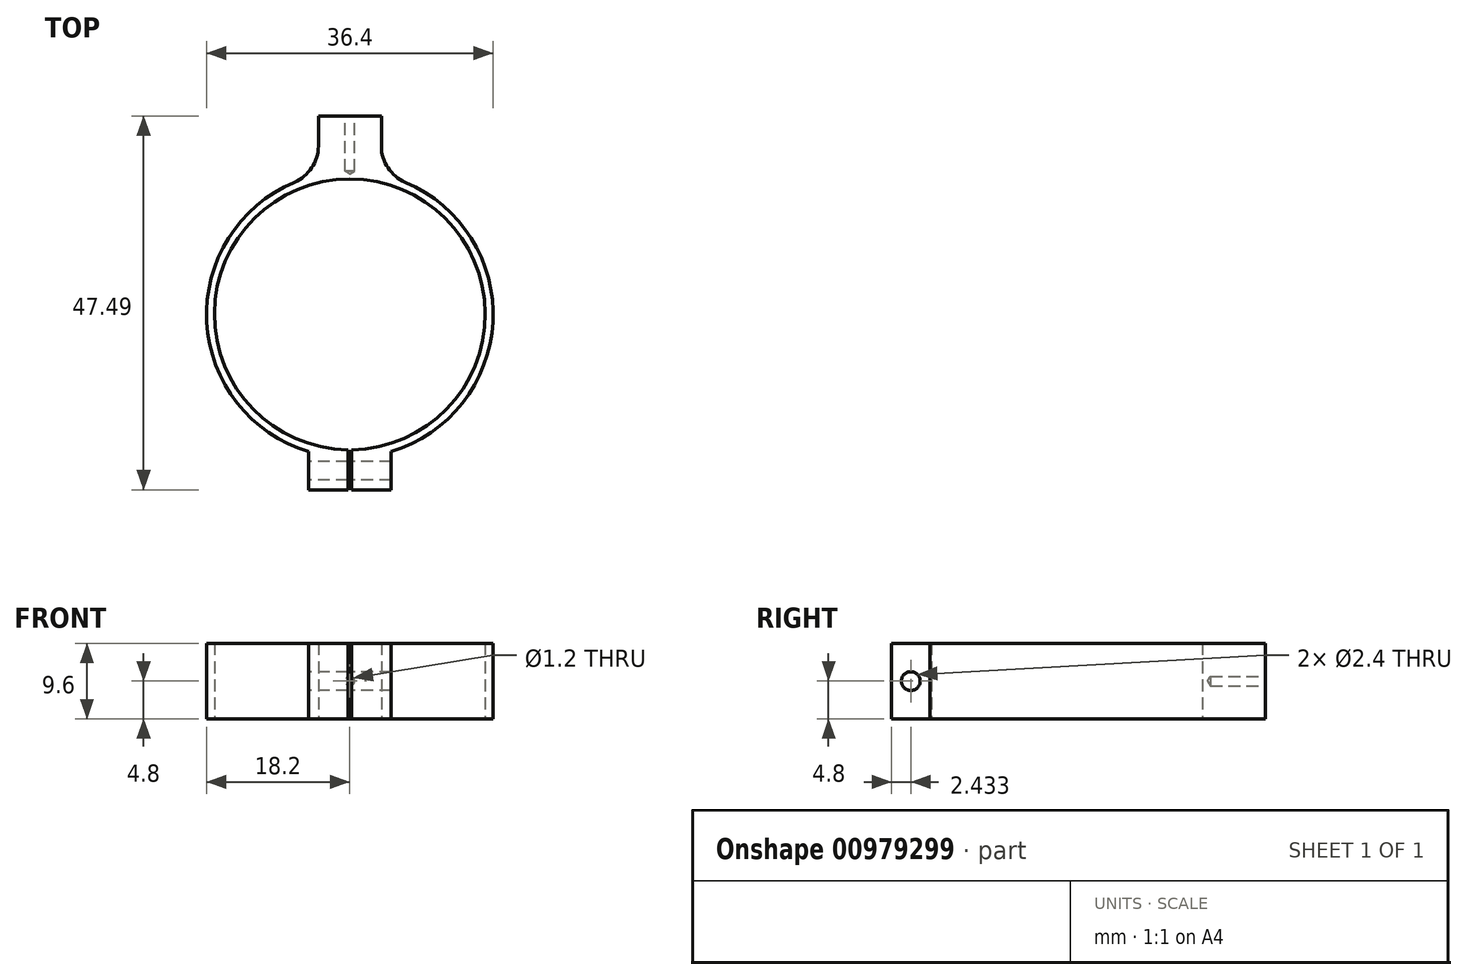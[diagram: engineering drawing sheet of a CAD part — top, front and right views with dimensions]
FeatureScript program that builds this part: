
annotation { "Feature Type Name" : "Feature", "Feature Type Description" : "" }
export const myFeature = defineFeature(function(context is Context, id is Id, definition is map)
    precondition{}
    {
        {
            var Q0;
            Q0=qCreatedBy(makeId("Top.planeOp"),FACE);
            var sketch = newSketch(context, id + "F0", { "sketchPlane" : qUnion([Q0])});
            skCircle(sketch, "E0", {"center": v(0, 0) * mm, "radius": 17.2 * mm});
            skArc(sketch, "E1.0", {"start": v(0.25, -18.2) * mm, "mid": v(0, 18.2) * mm, "end": v(-0.25, -18.2) * mm});
            skLineSegment(sketch, "E2", {"start": v(-4, 17.75) * mm, "end": v(-4, 25.2) * mm});
            skLineSegment(sketch, "E3", {"start": v(-4, 25.2) * mm, "end": v(4, 25.2) * mm});
            skLineSegment(sketch, "E4", {"start": v(4, 25.2) * mm, "end": v(4, 17.75) * mm});
            skLineSegment(sketch, "E5", {"start": v(0, 18.2) * mm, "end": v(0, 25.2) * mm, "construction": true});
            skLineSegment(sketch, "E6", {"start": v(-0.25, -18.2) * mm, "end": v(-0.25, -22.29) * mm});
            skLineSegment(sketch, "E7", {"start": v(-0.25, -22.29) * mm, "end": v(-5.25, -22.29) * mm});
            skLineSegment(sketch, "E8", {"start": v(-5.25, -22.29) * mm, "end": v(-5.25, -17.43) * mm});
            skLineSegment(sketch, "E9.MirrorCS", {"start": v(0.25, -18.2) * mm, "end": v(0.25, -22.29) * mm});
            skLineSegment(sketch, "E10.MirrorCS", {"start": v(0.25, -22.29) * mm, "end": v(5.25, -22.29) * mm});
            skLineSegment(sketch, "E11.MirrorCS", {"start": v(5.25, -22.29) * mm, "end": v(5.25, -17.43) * mm});
            skLineSegment(sketch, "E12", {"start": v(-0.25, -22.29) * mm, "end": v(0.25, -22.29) * mm, "construction": true});
            skLineSegment(sketch, "E13", {"start": v(-0.25, -18.2) * mm, "end": v(-0.25, -17.2) * mm});
            skLineSegment(sketch, "E14", {"start": v(0.25, -18.2) * mm, "end": v(0.25, -17.2) * mm});
            skSolve(sketch);
        }
        {
            var Q0;
            {var subQ0=sQuery(id+"F0.wireOp",EDGE,"E2");Q0=makeQuery(id+"F0.imprint","IMPRINT",FACE,{"disambiguationData":[TD([[makeQuery(id+"F0.imprint","IMPRINT",EDGE,{"derivedFrom":subQ0}),-1.0]])]});}
            var Q1;
            {var subQ5=sQuery(id+"F0.wireOp",EDGE,"E13");Q1=makeQuery(id+"F0.imprint","IMPRINT",FACE,{"disambiguationData":[TD([[makeQuery(id+"F0.imprint","IMPRINT",EDGE,{"derivedFrom":subQ5}),1.0]])]});}
            var Q2;
            {var subQ0=sQuery(id+"F0.wireOp",EDGE,"E6");Q2=makeQuery(id+"F0.imprint","IMPRINT",FACE,{"disambiguationData":[TD([[makeQuery(id+"F0.imprint","IMPRINT",EDGE,{"derivedFrom":subQ0}),-1.0]])]});}
            var Q3;
            {var subQ0=sQuery(id+"F0.wireOp",EDGE,"E9.MirrorCS");Q3=makeQuery(id+"F0.imprint","IMPRINT",FACE,{"disambiguationData":[TD([[makeQuery(id+"F0.imprint","IMPRINT",EDGE,{"derivedFrom":subQ0}),1.0]])]});}
            extrude(context, id + "F1", {"entities" : qUnion([Q0, Q1, Q2, Q3]), "depth" : 9.6 * mm, "offsetDistance" : 25 * mm});
        }
        {
            var Q0;
            Q0=makeQuery(id+"F1.opExtrude","SWEPT_FACE",FACE,{"disambiguationData":[OSD([sQuery(id+"F0.wireOp",EDGE,"E8")])]});
            var sketch = newSketch(context, id + "F2", { "sketchPlane" : qUnion([Q0])});
            skLineSegment(sketch, "E15", {"start": v(19.86, 9.6) * mm, "end": v(19.86, 0) * mm, "construction": true});
            skPoint(sketch, "E16", {"position": v(19.86, 4.8) * mm});
            skSolve(sketch);
        }
        {
            var Q0;
            Q0=sQuery(id+"F2.wireOp",VERTEX,"E16");
            var Q1;
            Q1=makeQuery(id+"F1.opExtrude","SWEPT_BODY",BODY,{"disambiguationData":[OSD([sQuery(id+"F0.wireOp",EDGE,"E0"),sQuery(id+"F0.wireOp",EDGE,"E1.0"),sQuery(id+"F0.wireOp",EDGE,"E2"),sQuery(id+"F0.wireOp",EDGE,"E3"),sQuery(id+"F0.wireOp",EDGE,"E4"),sQuery(id+"F0.wireOp",EDGE,"E6"),sQuery(id+"F0.wireOp",EDGE,"E7"),sQuery(id+"F0.wireOp",EDGE,"E8"),sQuery(id+"F0.wireOp",EDGE,"E9.MirrorCS"),sQuery(id+"F0.wireOp",EDGE,"E10.MirrorCS"),sQuery(id+"F0.wireOp",EDGE,"E11.MirrorCS"),sQuery(id+"F0.wireOp",EDGE,"E13"),sQuery(id+"F0.wireOp",EDGE,"E14")])]});
            hole(context, id + "F3", {"style" : HoleStyle.SIMPLE, "endStyle" : HoleEndStyle.THROUGH, "standardTappedOrClearance" : lookupTablePath({ "fit" : "Normal", "standard" : "ISO", "size" : "M2", "type" : "Clearance" }), "standardBlindInLast" : lookupTablePath({ "fit" : "Normal", "standard" : "ISO", "engagement" : "75%", "pitch" : "0.25 mm", "size" : "M2", "type" : "Clearance & tapped" }), "holeDiameter" : 2.4 * mm, "majorDiameter" : 5 * mm, "isTappedThrough" : true, "tappedDepth" : 12 * mm, "tapClearance" : 3, "locations" : qUnion([Q0]), "scope" : qUnion([Q1])});
        }
        {
            var Q0;
            Q0=makeQuery(id+"F1.opExtrude","SWEPT_FACE",FACE,{"disambiguationData":[OSD([sQuery(id+"F0.wireOp",EDGE,"E3")])]});
            var sketch = newSketch(context, id + "F4", { "sketchPlane" : qUnion([Q0])});
            skLineSegment(sketch, "E17", {"start": v(0, 0) * mm, "end": v(0, 9.6) * mm, "construction": true});
            skPoint(sketch, "E18", {"position": v(0, 4.8) * mm});
            skSolve(sketch);
        }
        {
            var Q0;
            Q0=sQuery(id+"F4.wireOp",VERTEX,"E18");
            var Q1;
            Q1=makeQuery(id+"F1.opExtrude","SWEPT_BODY",BODY,{"disambiguationData":[OSD([sQuery(id+"F0.wireOp",EDGE,"E0"),sQuery(id+"F0.wireOp",EDGE,"E1.0"),sQuery(id+"F0.wireOp",EDGE,"E2"),sQuery(id+"F0.wireOp",EDGE,"E3"),sQuery(id+"F0.wireOp",EDGE,"E4"),sQuery(id+"F0.wireOp",EDGE,"E6"),sQuery(id+"F0.wireOp",EDGE,"E7"),sQuery(id+"F0.wireOp",EDGE,"E8"),sQuery(id+"F0.wireOp",EDGE,"E9.MirrorCS"),sQuery(id+"F0.wireOp",EDGE,"E10.MirrorCS"),sQuery(id+"F0.wireOp",EDGE,"E11.MirrorCS"),sQuery(id+"F0.wireOp",EDGE,"E13"),sQuery(id+"F0.wireOp",EDGE,"E14")])]});
            hole(context, id + "F5", {"style" : HoleStyle.SIMPLE, "endStyle" : HoleEndStyle.BLIND, "standardTappedOrClearance" : lookupTablePath({ "fit" : "Normal", "standard" : "ISO", "size" : "M1", "type" : "Clearance" }), "standardBlindInLast" : lookupTablePath({ "fit" : "Normal", "standard" : "ISO", "engagement" : "75%", "pitch" : "0.2 mm", "size" : "M1", "type" : "Clearance & tapped" }), "holeDiameter" : 1.2 * mm, "majorDiameter" : 5 * mm, "holeDepth" : 7 * mm, "isTappedThrough" : true, "tappedDepth" : 12 * mm, "tapClearance" : 3, "locations" : qUnion([Q0]), "scope" : qUnion([Q1])});
        }
        {
            var Q0;
            Q0=makeQuery(id+"F1.opExtrude","SWEPT_EDGE",EDGE,{"disambiguationData":[OSD([sQuery(id+"F0.wireOp",EDGE,"E1.0"),sQuery(id+"F0.wireOp",EDGE,"E2")])]});
            var Q1;
            Q1=makeQuery(id+"F1.opExtrude","SWEPT_EDGE",EDGE,{"disambiguationData":[OSD([sQuery(id+"F0.wireOp",EDGE,"E1.0"),sQuery(id+"F0.wireOp",EDGE,"E4")])]});
            fillet(context, id + "F6", {"entities" : qUnion([Q0, Q1]), "radius" : 5 * mm, "tangentPropagation" : true, "allowEdgeOverflow" : false});
        }
    });
